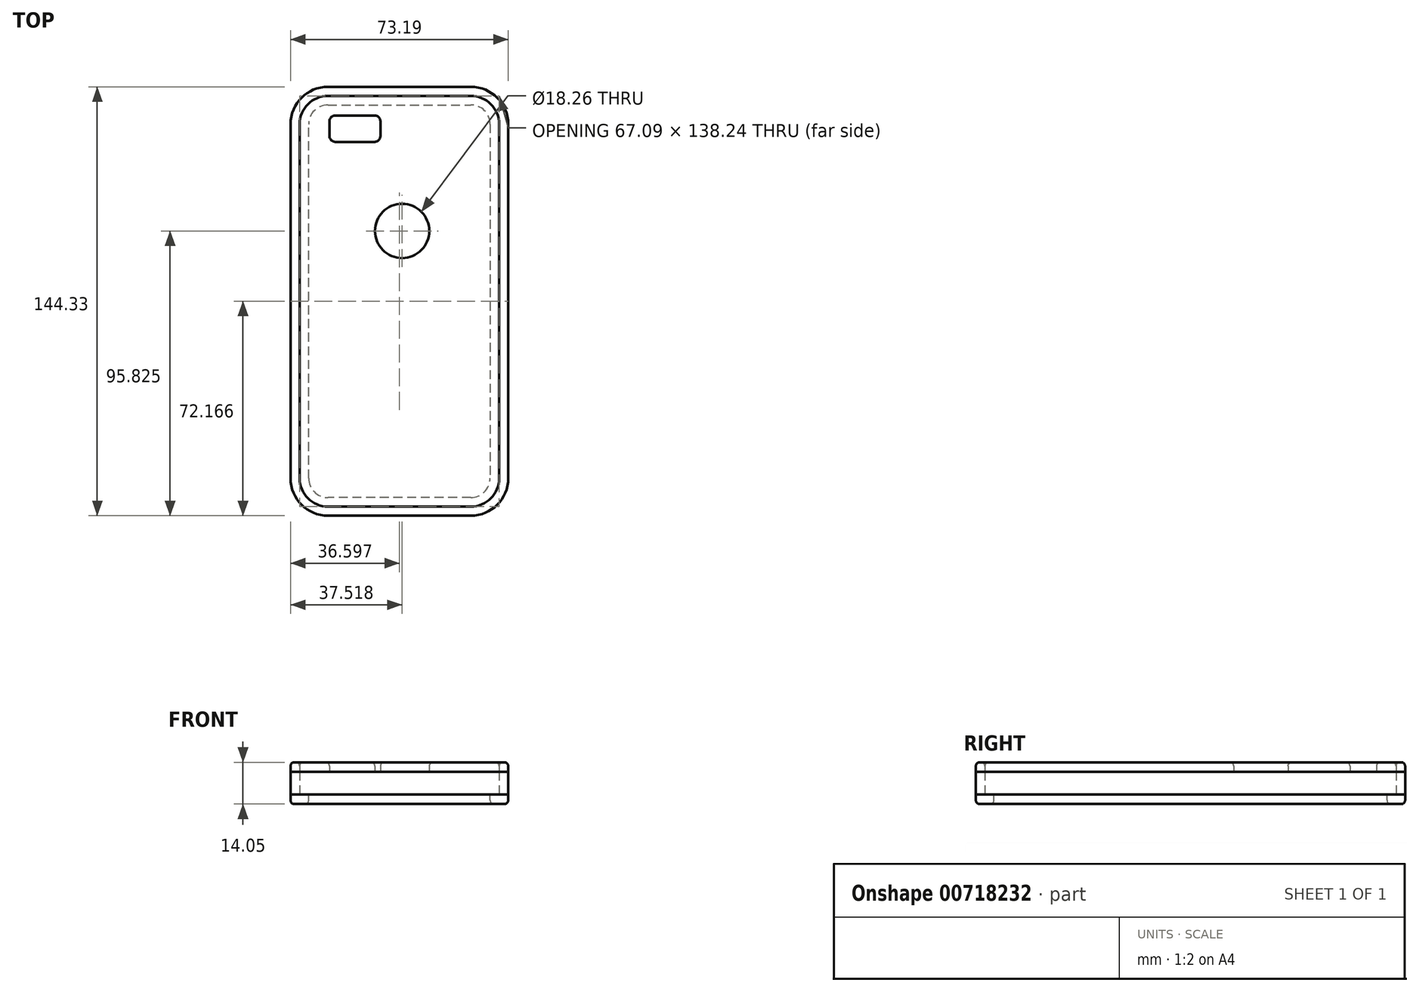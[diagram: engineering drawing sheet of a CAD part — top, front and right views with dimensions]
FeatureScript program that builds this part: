
annotation { "Feature Type Name" : "Feature", "Feature Type Description" : "" }
export const myFeature = defineFeature(function(context is Context, id is Id, definition is map)
    precondition{}
    {
        {
            var Q0;
            Q0=qCreatedBy(makeId("Top.planeOp"),FACE);
            var sketch = newSketch(context, id + "F0", { "sketchPlane" : qUnion([Q0])});
            skLineSegment(sketch, "E0", {"start": v(-36.43, 58.79) * mm, "end": v(11.6, 58.79) * mm});
            skLineSegment(sketch, "E1", {"start": v(21.13, 49.26) * mm, "end": v(21.13, -69.93) * mm});
            skLineSegment(sketch, "E2", {"start": v(11.6, -79.45) * mm, "end": v(-36.43, -79.45) * mm});
            skLineSegment(sketch, "E3", {"start": v(-45.96, -69.93) * mm, "end": v(-45.96, 49.26) * mm});
            skLineSegment(sketch, "E4", {"start": v(21.13, 49.26) * mm, "end": v(21.13, 29.72) * mm});
            skPoint(sketch, "E5.endSnap0", {"position": v(21.13, 44.25) * mm});
            skLineSegment(sketch, "E6", {"start": v(-35.93, 50.18) * mm, "end": v(-35.93, 45.32) * mm});
            skLineSegment(sketch, "E7", {"start": v(-33.9, 52.2) * mm, "end": v(-20.81, 52.2) * mm});
            skLineSegment(sketch, "E8", {"start": v(-18.78, 50.18) * mm, "end": v(-18.78, 45.32) * mm});
            skLineSegment(sketch, "E9", {"start": v(-20.81, 43.3) * mm, "end": v(-33.9, 43.3) * mm});
            skPoint(sketch, "E10.visualSharp", {"position": v(21.13, 58.79) * mm});
            skArc(sketch, "E10.filletArc", {"start": v(21.13, 49.26) * mm, "mid": v(18.34, 56) * mm, "end": v(11.6, 58.79) * mm});
            skPoint(sketch, "E11.visualSharp", {"position": v(-45.96, 58.79) * mm});
            skArc(sketch, "E11.filletArc", {"start": v(-36.43, 58.79) * mm, "mid": v(-43.17, 56) * mm, "end": v(-45.96, 49.26) * mm});
            skPoint(sketch, "E12.visualSharp", {"position": v(-45.96, -79.45) * mm});
            skArc(sketch, "E12.filletArc", {"start": v(-45.96, -69.93) * mm, "mid": v(-43.17, -76.66) * mm, "end": v(-36.43, -79.45) * mm});
            skPoint(sketch, "E13.visualSharp", {"position": v(21.13, -79.45) * mm});
            skArc(sketch, "E13.filletArc", {"start": v(11.6, -79.45) * mm, "mid": v(18.34, -76.66) * mm, "end": v(21.13, -69.93) * mm});
            skCircle(sketch, "E14", {"center": v(-11.5, 13.32) * mm, "radius": 9.13 * mm});
            skPoint(sketch, "E15.visualSharp", {"position": v(-35.93, 52.2) * mm});
            skArc(sketch, "E15.filletArc", {"start": v(-33.9, 52.2) * mm, "mid": v(-35.33, 51.61) * mm, "end": v(-35.93, 50.18) * mm});
            skPoint(sketch, "E16.visualSharp", {"position": v(-35.93, 43.3) * mm});
            skArc(sketch, "E16.filletArc", {"start": v(-35.93, 45.32) * mm, "mid": v(-35.33, 43.89) * mm, "end": v(-33.9, 43.3) * mm});
            skPoint(sketch, "E17.visualSharp", {"position": v(-18.78, 43.3) * mm});
            skArc(sketch, "E17.filletArc", {"start": v(-20.81, 43.3) * mm, "mid": v(-19.38, 43.89) * mm, "end": v(-18.78, 45.32) * mm});
            skPoint(sketch, "E18.visualSharp", {"position": v(-18.78, 52.2) * mm});
            skArc(sketch, "E18.filletArc", {"start": v(-18.78, 50.18) * mm, "mid": v(-19.38, 51.61) * mm, "end": v(-20.81, 52.2) * mm});
            skLineSegment(sketch, "E19.0", {"start": v(24.18, 49.26) * mm, "end": v(24.18, -69.93) * mm});
            skArc(sketch, "E19.1", {"start": v(11.6, -82.5) * mm, "mid": v(20.5, -78.82) * mm, "end": v(24.18, -69.93) * mm});
            skArc(sketch, "E19.2", {"start": v(24.18, 49.26) * mm, "mid": v(20.5, 58.15) * mm, "end": v(11.6, 61.83) * mm});
            skLineSegment(sketch, "E19.3", {"start": v(11.6, -82.5) * mm, "end": v(-36.43, -82.5) * mm});
            skLineSegment(sketch, "E19.4", {"start": v(-36.43, 61.83) * mm, "end": v(11.6, 61.83) * mm});
            skArc(sketch, "E19.5", {"start": v(-36.43, 61.83) * mm, "mid": v(-45.33, 58.15) * mm, "end": v(-49, 49.26) * mm});
            skLineSegment(sketch, "E19.6", {"start": v(-49, -69.93) * mm, "end": v(-49, 49.26) * mm});
            skArc(sketch, "E19.7", {"start": v(-49, -69.93) * mm, "mid": v(-45.33, -78.82) * mm, "end": v(-36.43, -82.5) * mm});
            skArc(sketch, "E20.0", {"start": v(-36.43, 55.74) * mm, "mid": v(-41.01, 53.84) * mm, "end": v(-42.91, 49.26) * mm});
            skLineSegment(sketch, "E20.1", {"start": v(-42.91, -69.93) * mm, "end": v(-42.91, 49.26) * mm});
            skLineSegment(sketch, "E20.2", {"start": v(-36.43, 55.74) * mm, "end": v(11.6, 55.74) * mm});
            skArc(sketch, "E20.3", {"start": v(-42.91, -69.93) * mm, "mid": v(-41.01, -74.5) * mm, "end": v(-36.43, -76.4) * mm});
            skArc(sketch, "E20.4", {"start": v(18.09, 49.26) * mm, "mid": v(16.19, 53.84) * mm, "end": v(11.6, 55.74) * mm});
            skLineSegment(sketch, "E20.5", {"start": v(18.09, 49.26) * mm, "end": v(18.09, -69.93) * mm});
            skArc(sketch, "E20.6", {"start": v(11.6, -76.4) * mm, "mid": v(16.19, -74.5) * mm, "end": v(18.09, -69.93) * mm});
            skLineSegment(sketch, "E20.7", {"start": v(11.6, -76.4) * mm, "end": v(-36.43, -76.4) * mm});
            skSolve(sketch);
        }
        {
            var Q0;
            Q0=makeQuery(id+"F0.imprint","IMPRINT",FACE,{"disambiguationData":[TD([[makeQuery(id+"F0.imprint","IMPRINT",EDGE,{"derivedFrom":sQuery(id+"F0.wireOp",EDGE,"E0")}),-1.0]])]});
            var Q1;
            Q1=makeQuery(id+"F0.imprint","IMPRINT",FACE,{"disambiguationData":[TD([[makeQuery(id+"F0.imprint","IMPRINT",EDGE,{"derivedFrom":sQuery(id+"F0.wireOp",EDGE,"E6")}),-1.0]])]});
            extrude(context, id + "F1", {"entities" : qUnion([Q0, Q1]), "depth" : 7.7 * mm, "offsetDistance" : 25.4 * mm});
        }
        {
            var Q0;
            Q0=makeQuery(id+"F1.opExtrude","SWEPT_FACE",FACE,{"disambiguationData":[OSD([sQuery(id+"F0.wireOp",EDGE,"E3")])]});
            var sketch = newSketch(context, id + "F2", { "sketchPlane" : qUnion([Q0])});
            skLineSegment(sketch, "E21.0", {"start": v(-58.79, 7.7) * mm, "end": v(-58.79, 0) * mm});
            skLineSegment(sketch, "E22", {"start": v(-58.79, 0) * mm, "end": v(-30.21, 0) * mm});
            skLineSegment(sketch, "E23", {"start": v(-30.21, 0) * mm, "end": v(-30.21, 1.98) * mm});
            skLineSegment(sketch, "E24", {"start": v(-30.21, 1.98) * mm, "end": v(-20.43, 1.98) * mm});
            skLineSegment(sketch, "E25", {"start": v(-20.43, 1.98) * mm, "end": v(-20.43, 3.97) * mm});
            skLineSegment(sketch, "E26", {"start": v(-20.43, 3.97) * mm, "end": v(-30.21, 3.97) * mm});
            skLineSegment(sketch, "E27", {"start": v(-30.21, 3.97) * mm, "end": v(-30.21, 1.98) * mm});
            skSolve(sketch);
        }
        {
            var Q0;
            Q0 = qSketchRegion(id + "F2", true);
            extrude(context, id + "F3", {"entities" : qUnion([Q0]), "depth" : 9.14 * mm, "offsetDistance" : 25.4 * mm});
        }
        {
            var Q0;
            Q0=makeQuery(id+"F1.opExtrude","SWEPT_FACE",FACE,{"disambiguationData":[OSD([sQuery(id+"F0.wireOp",EDGE,"E2")])]});
            var sketch = newSketch(context, id + "F4", { "sketchPlane" : qUnion([Q0])});
            skLineSegment(sketch, "E28", {"start": v(-34.7, 6.68) * mm, "end": v(9.6, 6.68) * mm});
            skLineSegment(sketch, "E29", {"start": v(9.6, 6.68) * mm, "end": v(9.6, 1.25) * mm});
            skLineSegment(sketch, "E30", {"start": v(9.6, 1.25) * mm, "end": v(-34.7, 1.25) * mm});
            skLineSegment(sketch, "E31", {"start": v(-34.7, 1.25) * mm, "end": v(-34.7, 6.68) * mm});
            skSolve(sketch);
        }
        {
            var Q0;
            Q0 = qSketchRegion(id + "F4", true);
            extrude(context, id + "F5", {"entities" : qUnion([Q0]), "operationType" : NewBodyOperationType.ADD, "depth" : 17.02 * mm, "offsetDistance" : 25.4 * mm});
        }
        {
            var Q0;
            Q0=qCreatedBy(makeId("Right.planeOp"),FACE);
            var sketch = newSketch(context, id + "F6", { "sketchPlane" : qUnion([Q0])});
            skLineSegment(sketch, "E32", {"start": v(60.1, 0) * mm, "end": v(41.85, 0) * mm});
            skLineSegment(sketch, "E33", {"start": v(41.85, 0) * mm, "end": v(41.85, 1.98) * mm});
            skLineSegment(sketch, "E34", {"start": v(41.85, 1.98) * mm, "end": v(6.93, 1.98) * mm});
            skLineSegment(sketch, "E35", {"start": v(6.93, 1.98) * mm, "end": v(6.93, 3.97) * mm});
            skLineSegment(sketch, "E36", {"start": v(6.93, 3.97) * mm, "end": v(41.85, 3.97) * mm});
            skLineSegment(sketch, "E37", {"start": v(41.85, 3.97) * mm, "end": v(41.85, 1.98) * mm});
            skSolve(sketch);
        }
        {
            var Q0;
            Q0 = qSketchRegion(id + "F6", true);
            extrude(context, id + "F7", {"entities" : qUnion([Q0]), "depth" : 68.83 * mm, "offsetDistance" : 25.4 * mm});
        }
        {
            var Q0;
            Q0=makeQuery(id+"F0.imprint","IMPRINT",FACE,{"disambiguationData":[TD([[makeQuery(id+"F0.imprint","IMPRINT",EDGE,{"derivedFrom":sQuery(id+"F0.wireOp",EDGE,"E0")}),1.0]])]});
            var Q1;
            Q1=makeQuery(id+"F1.opExtrude","CAP_FACE",FACE,{"disambiguationData":[OSD([sQuery(id+"F0.wireOp",EDGE,"E0"),sQuery(id+"F0.wireOp",EDGE,"E1"),sQuery(id+"F0.wireOp",EDGE,"E2"),sQuery(id+"F0.wireOp",EDGE,"E3"),sQuery(id+"F0.wireOp",EDGE,"E4"),sQuery(id+"F0.wireOp",EDGE,"E6"),sQuery(id+"F0.wireOp",EDGE,"E7"),sQuery(id+"F0.wireOp",EDGE,"E8"),sQuery(id+"F0.wireOp",EDGE,"E9"),sQuery(id+"F0.wireOp",EDGE,"E10.filletArc"),sQuery(id+"F0.wireOp",EDGE,"E11.filletArc"),sQuery(id+"F0.wireOp",EDGE,"E12.filletArc"),sQuery(id+"F0.wireOp",EDGE,"E13.filletArc"),sQuery(id+"F0.wireOp",EDGE,"E14"),sQuery(id+"F0.wireOp",EDGE,"E15.filletArc"),sQuery(id+"F0.wireOp",EDGE,"E16.filletArc"),sQuery(id+"F0.wireOp",EDGE,"E17.filletArc"),sQuery(id+"F0.wireOp",EDGE,"E18.filletArc")])],"isStart":false});
            extrude(context, id + "F8", {"entities" : qUnion([Q0]), "endBound" : BoundingType.UP_TO_SURFACE, "depth" : 25.4 * mm, "endBoundEntityFace" : qUnion([Q1]), "offsetDistance" : 25.4 * mm});
        }
        {
            var Q0;
            Q0=makeQuery(id+"F0.imprint","IMPRINT",FACE,{"disambiguationData":[TD([[makeQuery(id+"F0.imprint","IMPRINT",EDGE,{"derivedFrom":sQuery(id+"F0.wireOp",EDGE,"E6")}),-1.0]])]});
            extrude(context, id + "F9", {"entities" : qUnion([Q0]), "operationType" : NewBodyOperationType.ADD, "oppositeDirection" : true, "depth" : 32 * mm, "offsetDistance" : 25.4 * mm});
        }
        {
            var Q0;
            Q0=makeQuery(id+"F0.imprint","IMPRINT",FACE,{"disambiguationData":[TD([[makeQuery(id+"F0.imprint","IMPRINT",EDGE,{"derivedFrom":sQuery(id+"F0.wireOp",EDGE,"E0")}),-1.0]])]});
            var Q1;
            Q1=makeQuery(id+"F0.imprint","IMPRINT",FACE,{"disambiguationData":[TD([[makeQuery(id+"F0.imprint","IMPRINT",EDGE,{"derivedFrom":sQuery(id+"F0.wireOp",EDGE,"E0")}),1.0]])]});
            extrude(context, id + "F10", {"entities" : qUnion([Q0, Q1]), "oppositeDirection" : true, "depth" : 3.17 * mm, "offsetDistance" : 25.4 * mm});
        }
        {
            var Q0;
            Q0=makeQuery(id+"F1.opExtrude","CAP_FACE",FACE,{"disambiguationData":[OSD([sQuery(id+"F0.wireOp",EDGE,"E0"),sQuery(id+"F0.wireOp",EDGE,"E1"),sQuery(id+"F0.wireOp",EDGE,"E2"),sQuery(id+"F0.wireOp",EDGE,"E3"),sQuery(id+"F0.wireOp",EDGE,"E4"),sQuery(id+"F0.wireOp",EDGE,"E6"),sQuery(id+"F0.wireOp",EDGE,"E7"),sQuery(id+"F0.wireOp",EDGE,"E8"),sQuery(id+"F0.wireOp",EDGE,"E9"),sQuery(id+"F0.wireOp",EDGE,"E10.filletArc"),sQuery(id+"F0.wireOp",EDGE,"E11.filletArc"),sQuery(id+"F0.wireOp",EDGE,"E12.filletArc"),sQuery(id+"F0.wireOp",EDGE,"E13.filletArc"),sQuery(id+"F0.wireOp",EDGE,"E14"),sQuery(id+"F0.wireOp",EDGE,"E15.filletArc"),sQuery(id+"F0.wireOp",EDGE,"E16.filletArc"),sQuery(id+"F0.wireOp",EDGE,"E17.filletArc"),sQuery(id+"F0.wireOp",EDGE,"E18.filletArc")])],"isStart":false});
            var Q1;
            Q1=makeQuery(id+"F8.opExtrude","CAP_FACE",FACE,{"disambiguationData":[OSD([sQuery(id+"F0.wireOp",EDGE,"E0"),sQuery(id+"F0.wireOp",EDGE,"E1"),sQuery(id+"F0.wireOp",EDGE,"E2"),sQuery(id+"F0.wireOp",EDGE,"E3"),sQuery(id+"F0.wireOp",EDGE,"E4"),sQuery(id+"F0.wireOp",EDGE,"E6"),sQuery(id+"F0.wireOp",EDGE,"E7"),sQuery(id+"F0.wireOp",EDGE,"E8"),sQuery(id+"F0.wireOp",EDGE,"E9"),sQuery(id+"F0.wireOp",EDGE,"E10.filletArc"),sQuery(id+"F0.wireOp",EDGE,"E11.filletArc"),sQuery(id+"F0.wireOp",EDGE,"E12.filletArc"),sQuery(id+"F0.wireOp",EDGE,"E13.filletArc"),sQuery(id+"F0.wireOp",EDGE,"E14"),sQuery(id+"F0.wireOp",EDGE,"E15.filletArc"),sQuery(id+"F0.wireOp",EDGE,"E16.filletArc"),sQuery(id+"F0.wireOp",EDGE,"E17.filletArc"),sQuery(id+"F0.wireOp",EDGE,"E18.filletArc")])],"isStart":false});
            extrude(context, id + "F11", {"entities" : qUnion([Q0, Q1]), "depth" : 3.17 * mm, "offsetDistance" : 25.4 * mm});
        }
        {
            var Q0;
            Q0=makeQuery(id+"F3.opExtrude","SWEPT_BODY",BODY,{"disambiguationData":[OSD([sQuery(id+"F2.wireOp",EDGE,"E24"),sQuery(id+"F2.wireOp",EDGE,"E25"),sQuery(id+"F2.wireOp",EDGE,"E26"),sQuery(id+"F2.wireOp",EDGE,"E27")])]});
            var Q1;
            Q1=makeQuery(id+"F7.opExtrude","SWEPT_BODY",BODY,{"disambiguationData":[OSD([sQuery(id+"F6.wireOp",EDGE,"E34"),sQuery(id+"F6.wireOp",EDGE,"E35"),sQuery(id+"F6.wireOp",EDGE,"E36"),sQuery(id+"F6.wireOp",EDGE,"E37")])]});
            var Q2;
            Q2=makeQuery(id+"F1.opExtrude","SWEPT_BODY",BODY,{"disambiguationData":[OSD([sQuery(id+"F0.wireOp",EDGE,"E0"),sQuery(id+"F0.wireOp",EDGE,"E1"),sQuery(id+"F0.wireOp",EDGE,"E2"),sQuery(id+"F0.wireOp",EDGE,"E3"),sQuery(id+"F0.wireOp",EDGE,"E4"),sQuery(id+"F0.wireOp",EDGE,"E6"),sQuery(id+"F0.wireOp",EDGE,"E7"),sQuery(id+"F0.wireOp",EDGE,"E8"),sQuery(id+"F0.wireOp",EDGE,"E9"),sQuery(id+"F0.wireOp",EDGE,"E10.filletArc"),sQuery(id+"F0.wireOp",EDGE,"E11.filletArc"),sQuery(id+"F0.wireOp",EDGE,"E12.filletArc"),sQuery(id+"F0.wireOp",EDGE,"E13.filletArc"),sQuery(id+"F0.wireOp",EDGE,"E14"),sQuery(id+"F0.wireOp",EDGE,"E15.filletArc"),sQuery(id+"F0.wireOp",EDGE,"E16.filletArc"),sQuery(id+"F0.wireOp",EDGE,"E17.filletArc"),sQuery(id+"F0.wireOp",EDGE,"E18.filletArc")])]});
            var Q3;
            {var subQ0=sQuery(id+"F0.wireOp",EDGE,"E18.filletArc");var subQ1=sQuery(id+"F0.wireOp",EDGE,"E17.filletArc");var subQ2=sQuery(id+"F0.wireOp",EDGE,"E16.filletArc");var subQ3=sQuery(id+"F0.wireOp",EDGE,"E15.filletArc");var subQ4=sQuery(id+"F0.wireOp",EDGE,"E14");var subQ5=sQuery(id+"F0.wireOp",EDGE,"E13.filletArc");var subQ6=sQuery(id+"F0.wireOp",EDGE,"E12.filletArc");var subQ7=sQuery(id+"F0.wireOp",EDGE,"E11.filletArc");var subQ8=sQuery(id+"F0.wireOp",EDGE,"E10.filletArc");var subQ9=sQuery(id+"F0.wireOp",EDGE,"E9");var subQ10=sQuery(id+"F0.wireOp",EDGE,"E8");var subQ11=sQuery(id+"F0.wireOp",EDGE,"E7");var subQ12=sQuery(id+"F0.wireOp",EDGE,"E6");var subQ13=sQuery(id+"F0.wireOp",EDGE,"E4");var subQ14=sQuery(id+"F0.wireOp",EDGE,"E3");var subQ15=sQuery(id+"F0.wireOp",EDGE,"E2");var subQ16=sQuery(id+"F0.wireOp",EDGE,"E1");var subQ17=sQuery(id+"F0.wireOp",EDGE,"E0");Q3=makeQuery(id+"F11.opExtrude","SWEPT_BODY",BODY,{"disambiguationData":[OSD([subQ17,subQ16,subQ15,subQ14,subQ13,subQ12,subQ11,subQ10,subQ9,subQ8,subQ7,subQ6,subQ5,subQ4,subQ3,subQ2,subQ1,subQ0]),TDD([makeQuery(id+"F1.opExtrude","CAP_FACE",FACE,{"disambiguationData":[OSD([subQ17,subQ16,subQ15,subQ14,subQ13,subQ12,subQ11,subQ10,subQ9,subQ8,subQ7,subQ6,subQ5,subQ4,subQ3,subQ2,subQ1,subQ0])],"isStart":false})])]});}
            booleanBodies(context, id + "F12", {"operationType" : BooleanOperationType.SUBTRACTION, "tools" : qUnion([Q0, Q1, Q2]), "targets" : qUnion([Q3])});
        }
        {
            var Q0;
            Q0=makeQuery(id+"F10.opExtrude","CAP_EDGE",EDGE,{"disambiguationData":[OSD([sQuery(id+"F0.wireOp",EDGE,"E19.6")])],"isStart":false});
            var Q1;
            Q1=makeQuery(id+"F10.opExtrude","CAP_EDGE",EDGE,{"disambiguationData":[OSD([sQuery(id+"F0.wireOp",EDGE,"E19.7")])],"isStart":false});
            var Q2;
            Q2=makeQuery(id+"F11.opExtrude","CAP_EDGE",EDGE,{"disambiguationData":[OSD([sQuery(id+"F0.wireOp",EDGE,"E0"),sQuery(id+"F0.wireOp",EDGE,"E1"),sQuery(id+"F0.wireOp",EDGE,"E2"),sQuery(id+"F0.wireOp",EDGE,"E3"),sQuery(id+"F0.wireOp",EDGE,"E4"),sQuery(id+"F0.wireOp",EDGE,"E6"),sQuery(id+"F0.wireOp",EDGE,"E7"),sQuery(id+"F0.wireOp",EDGE,"E8"),sQuery(id+"F0.wireOp",EDGE,"E9"),sQuery(id+"F0.wireOp",EDGE,"E10.filletArc"),sQuery(id+"F0.wireOp",EDGE,"E11.filletArc"),sQuery(id+"F0.wireOp",EDGE,"E12.filletArc"),sQuery(id+"F0.wireOp",EDGE,"E13.filletArc"),sQuery(id+"F0.wireOp",EDGE,"E14"),sQuery(id+"F0.wireOp",EDGE,"E15.filletArc"),sQuery(id+"F0.wireOp",EDGE,"E16.filletArc"),sQuery(id+"F0.wireOp",EDGE,"E17.filletArc"),sQuery(id+"F0.wireOp",EDGE,"E18.filletArc"),sQuery(id+"F0.wireOp",EDGE,"E19.6")])],"isStart":false});
            var Q3;
            Q3=makeQuery(id+"F10.opExtrude","CAP_EDGE",EDGE,{"disambiguationData":[OSD([sQuery(id+"F0.wireOp",EDGE,"E20.2")])],"isStart":false});
            fillet(context, id + "F13", {"entities" : qUnion([Q0, Q1, Q2, Q3]), "radius" : 1.27 * mm, "tangentPropagation" : true, "allowEdgeOverflow" : false});
        }
    });
